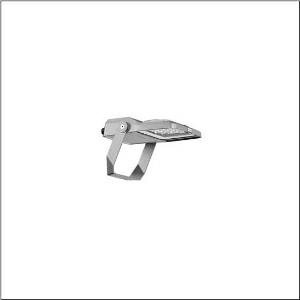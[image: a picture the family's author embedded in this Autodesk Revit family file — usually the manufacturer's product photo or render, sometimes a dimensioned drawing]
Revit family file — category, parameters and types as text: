
# Revit family: floodlight_fl_21_micro___rs12_5xa7762a2b1a_e5c3
name_source: partatom
category: Lighting Fixtures
units: mm (PartAtom-declared; Revit-internal decimal feet)

## family parameters
Cut with Voids When Loaded = No
Host = Face
Light Source = No
Part Type = Normal
Room Calculation Point = No
Round Connector Dimension = Use Diameter
Shared = No

## types (1)
- --- (1 x LED, 3090 lm, 23.1 W, 3000K)
    Apparent Load = 23 VA
    CIE Flux Codes = 79 92 99 100 100
    Color Rendering = 70
    Color Temperature = 3000K
    Default Elevation = 1800 mm
    Description = Floodlight FL 21 micro, floodlight, primary light control with lens, of PMMA, primary optical cover: protective disc, of toughened safety glass, transparent, light distribution: RS12, light emission: direct distribution, installation type: surface-mounted, LED, High Power LED, rated luminous flux: 3.090lm, luminous efficacy: 134lm/W, light colour: 730, colour temperature: 3000K, control gear: ECG iQ, control: Auto-Match, Temp-Guard, Night-Set, Smart-Wire, Desk-Remote (wireless, voltage-free reading and setting of iQ features in the workshop via application-optimized NFC function/RFID function), optimised constant luminous flux control (CLO 2.0), Street-Remote, with terminal, 6-pole, mains connection: 220..240V, AC, 50/60Hz, start of lifetime: 23W, end of lifetime: 24W, reduction: 11W, luminaire housing, of diecast aluminium, powder-coated, Siteco® metallic grey (DB 702S), corrosivity category C5 according to DIN EN ISO 12944, mounting bracket, of steel, galvanised, powder-coated, Siteco® metallic grey (DB 702S), protection rating (complete): IP66, insulation class (complete): insulation class II (safety insulation), certification: CE, protection symbol: D, impact resistance: IK07, permissible operating ambient temperature: -40..+40°C, permissible operating ambient temperature for outdoor applications: -40..+50°C, standard: DIN EN 12944, packaging unit: 1 piece

Light Distribution: RS12
    Height = 65 mm
    Lamp = 1 x LED
    Lamp Light Flux = 3090 lm
    Lamp Power = 23.1 W
    Lamp count = 1
    Length = 312 mm
    Luminous efficacy = 134 lm/W
    Manufacturer = Siteco
    ModVariant = No
    Model = 5XA7762A2B1A
    Number of Poles = 1
    OnlyDefault = Yes
    Power Factor = 1
    Product Name = Floodlight FL 21 micro | RS12
    Product group = floodlight | pylon top
    ProductGroupID = 6101
    Protection Class = Protection class II
    Protection Degree = IP 66
    RLX_Detail_Level = 1
    RlxData = <blob elided: 74933 chars, md5=b0c67839>
    Socket = socket
    Standby Power = 0 W
    System Light Flux = 3090 lm
    System Power = 23 W
    Type Comments = factory setting: luminous flux: 100 % | dim-lin: 254 | 455 mA
    Type Image = l_1006880.jpg
    URL = http://relux.com
    VarID = @adj_095463
    Voltage = 0 V
    Weight = 0.00 kg
    Width = 230 mm

## geometry (parser evidence)
native form markers: Blend x4, Sweep x12
no freeform markers — native parametric forms only
